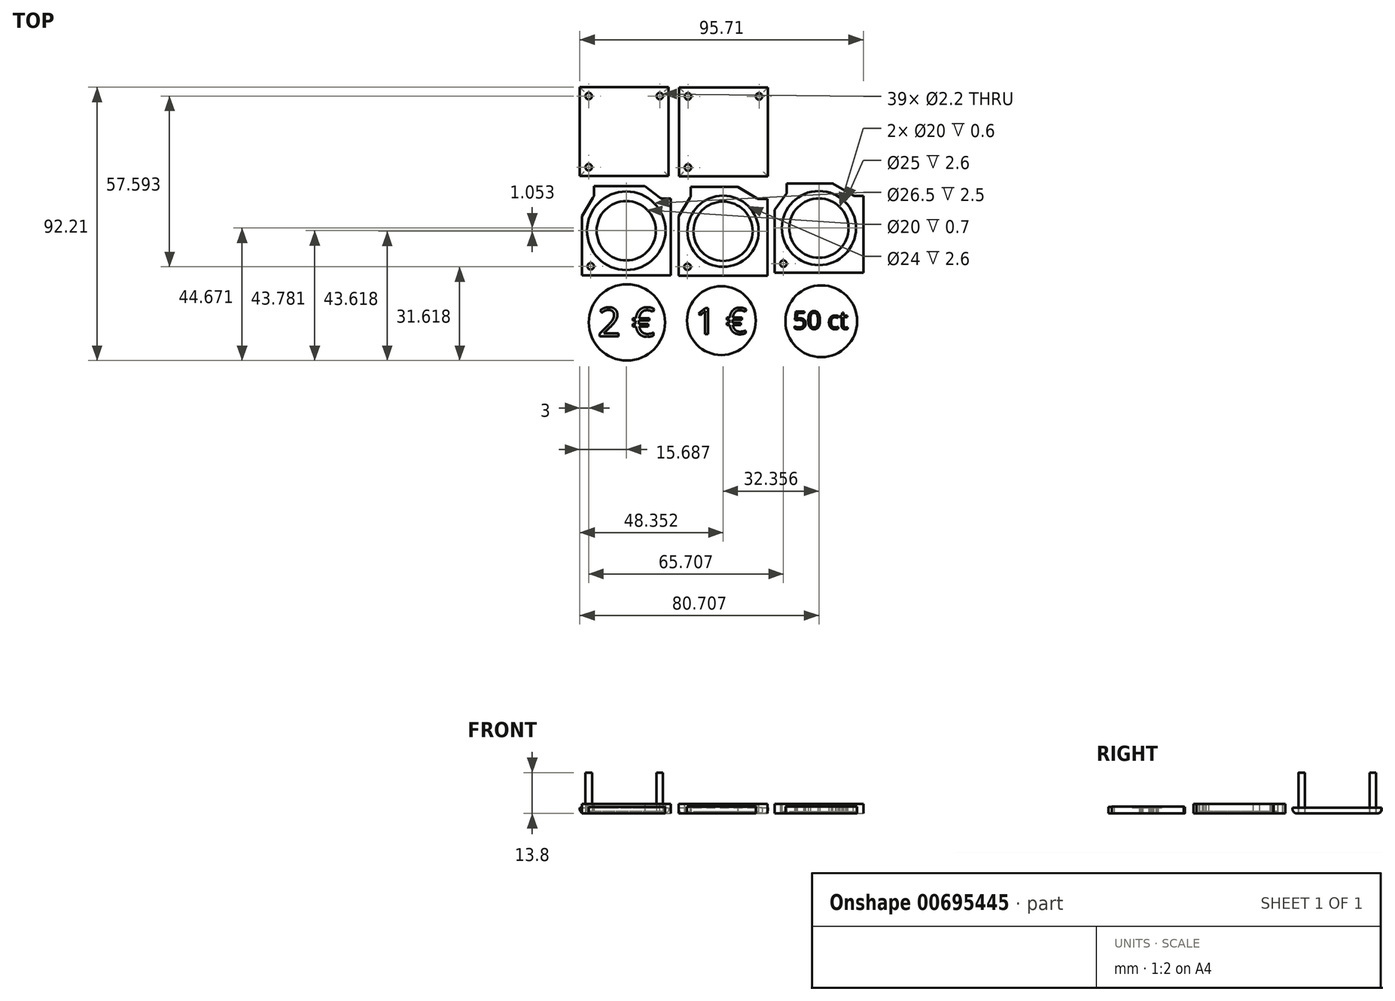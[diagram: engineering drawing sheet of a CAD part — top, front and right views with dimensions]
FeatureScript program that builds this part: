
annotation { "Feature Type Name" : "Feature", "Feature Type Description" : "" }
export const myFeature = defineFeature(function(context is Context, id is Id, definition is map)
    precondition{}
    {
        {
            var Q0;
            Q0=qCreatedBy(makeId("Top.planeOp"),FACE);
            var sketch = newSketch(context, id + "F0", { "sketchPlane" : qUnion([Q0])});
            skLineSegment(sketch, "E0.bottom", {"start": v(-47.79, 46.52) * mm, "end": v(-17.79, 46.52) * mm});
            skLineSegment(sketch, "E0.top", {"start": v(-47.79, 16.52) * mm, "end": v(-17.79, 16.52) * mm});
            skLineSegment(sketch, "E0.left", {"start": v(-47.79, 46.52) * mm, "end": v(-47.79, 16.52) * mm});
            skLineSegment(sketch, "E0.right", {"start": v(-17.79, 46.52) * mm, "end": v(-17.79, 16.52) * mm});
            skCircle(sketch, "E1", {"center": v(-44.79, 43.52) * mm, "radius": 1.1 * mm});
            skCircle(sketch, "E2", {"center": v(-20.79, 43.52) * mm, "radius": 1.1 * mm});
            skCircle(sketch, "E3", {"center": v(-44.79, 19.52) * mm, "radius": 1.1 * mm});
            skSolve(sketch);
        }
        {
            var Q0;
            Q0=makeQuery(id+"F0.imprint","IMPRINT",FACE,{"disambiguationData":[TD([[makeQuery(id+"F0.imprint","IMPRINT",EDGE,{"derivedFrom":sQuery(id+"F0.wireOp",EDGE,"E1")}),1.0]])]});
            var Q1;
            Q1=makeQuery(id+"F0.imprint","IMPRINT",FACE,{"disambiguationData":[TD([[makeQuery(id+"F0.imprint","IMPRINT",EDGE,{"derivedFrom":sQuery(id+"F0.wireOp",EDGE,"E2")}),1.0]])]});
            var Q2;
            Q2=makeQuery(id+"F0.imprint","IMPRINT",FACE,{"disambiguationData":[TD([[makeQuery(id+"F0.imprint","IMPRINT",EDGE,{"derivedFrom":sQuery(id+"F0.wireOp",EDGE,"E3")}),1.0]])]});
            extrude(context, id + "F1", {"entities" : qUnion([Q0, Q1, Q2]), "depth" : 13.8 * mm, "offsetDistance" : 25 * mm});
        }
        {
            var Q0;
            Q0 = qSketchRegion(id + "F0", true);
            extrude(context, id + "F2", {"entities" : qUnion([Q0]), "depth" : 2 * mm, "offsetDistance" : 25 * mm});
        }
        {
            var Q0;
            Q0=qCreatedBy(makeId("Top.planeOp"),FACE);
            var sketch = newSketch(context, id + "F3", { "sketchPlane" : qUnion([Q0])});
            skLineSegment(sketch, "E4.bottom", {"start": v(-14.28, 46.4) * mm, "end": v(15.72, 46.4) * mm});
            skLineSegment(sketch, "E4.top", {"start": v(-14.28, 16.4) * mm, "end": v(15.72, 16.4) * mm});
            skLineSegment(sketch, "E4.left", {"start": v(-14.28, 46.4) * mm, "end": v(-14.28, 16.4) * mm});
            skLineSegment(sketch, "E4.right", {"start": v(15.72, 46.4) * mm, "end": v(15.72, 16.4) * mm});
            skCircle(sketch, "E5", {"center": v(-11.28, 43.4) * mm, "radius": 1.1 * mm});
            skCircle(sketch, "E6", {"center": v(12.72, 43.4) * mm, "radius": 1.1 * mm});
            skCircle(sketch, "E7", {"center": v(-11.28, 19.4) * mm, "radius": 1.1 * mm});
            skSolve(sketch);
        }
        {
            var Q0;
            Q0=makeQuery(id+"F3.imprint","IMPRINT",FACE,{"disambiguationData":[TD([[makeQuery(id+"F3.imprint","IMPRINT",EDGE,{"derivedFrom":sQuery(id+"F3.wireOp",EDGE,"E5")}),1.0]])]});
            var Q1;
            Q1=makeQuery(id+"F3.imprint","IMPRINT",FACE,{"disambiguationData":[TD([[makeQuery(id+"F3.imprint","IMPRINT",EDGE,{"derivedFrom":sQuery(id+"F3.wireOp",EDGE,"E6")}),1.0]])]});
            var Q2;
            Q2=makeQuery(id+"F3.imprint","IMPRINT",FACE,{"disambiguationData":[TD([[makeQuery(id+"F3.imprint","IMPRINT",EDGE,{"derivedFrom":sQuery(id+"F3.wireOp",EDGE,"E7")}),1.0]])]});
            extrude(context, id + "F4", {"entities" : qUnion([Q0, Q1, Q2]), "depth" : 0.2 * mm, "offsetDistance" : 25 * mm});
        }
        {
            var Q0;
            Q0 = qSketchRegion(id + "F3", true);
            extrude(context, id + "F5", {"entities" : qUnion([Q0]), "depth" : 2 * mm, "offsetDistance" : 25 * mm});
        }
        {
            var Q0;
            Q0=makeQuery(id+"F2.opExtrude","CAP_EDGE",EDGE,{"disambiguationData":[OSD([sQuery(id+"F0.wireOp",EDGE,"E0.left")])],"isStart":true});
            var Q1;
            Q1=makeQuery(id+"F2.opExtrude","CAP_EDGE",EDGE,{"disambiguationData":[OSD([sQuery(id+"F0.wireOp",EDGE,"E0.bottom")])],"isStart":true});
            var Q2;
            Q2=makeQuery(id+"F2.opExtrude","CAP_EDGE",EDGE,{"disambiguationData":[OSD([sQuery(id+"F0.wireOp",EDGE,"E0.right")])],"isStart":true});
            var Q3;
            Q3=makeQuery(id+"F2.opExtrude","CAP_EDGE",EDGE,{"disambiguationData":[OSD([sQuery(id+"F0.wireOp",EDGE,"E0.top")])],"isStart":true});
            var Q4;
            Q4=makeQuery(id+"F5.opExtrude","CAP_EDGE",EDGE,{"disambiguationData":[OSD([sQuery(id+"F3.wireOp",EDGE,"E4.left")])],"isStart":true});
            var Q5;
            Q5=makeQuery(id+"F5.opExtrude","CAP_EDGE",EDGE,{"disambiguationData":[OSD([sQuery(id+"F3.wireOp",EDGE,"E4.bottom")])],"isStart":true});
            var Q6;
            Q6=makeQuery(id+"F5.opExtrude","CAP_EDGE",EDGE,{"disambiguationData":[OSD([sQuery(id+"F3.wireOp",EDGE,"E4.right")])],"isStart":true});
            var Q7;
            Q7=makeQuery(id+"F5.opExtrude","CAP_EDGE",EDGE,{"disambiguationData":[OSD([sQuery(id+"F3.wireOp",EDGE,"E4.top")])],"isStart":true});
            fillet(context, id + "F6", {"entities" : qUnion([Q0, Q1, Q2, Q3, Q4, Q5, Q6, Q7]), "radius" : 1.5 * mm, "tangentPropagation" : true, "allowEdgeOverflow" : false});
        }
        {
            var Q0;
            Q0=qCreatedBy(makeId("Top.planeOp"),FACE);
            var sketch = newSketch(context, id + "F7", { "sketchPlane" : qUnion([Q0])});
            skLineSegment(sketch, "E8.bottom", {"start": v(-47.1, 13.1) * mm, "end": v(-17.1, 13.1) * mm});
            skLineSegment(sketch, "E8.top", {"start": v(-47.1, -16.9) * mm, "end": v(-17.1, -16.9) * mm});
            skLineSegment(sketch, "E8.left", {"start": v(-47.1, 13.1) * mm, "end": v(-47.1, -16.9) * mm});
            skLineSegment(sketch, "E8.right", {"start": v(-17.1, 13.1) * mm, "end": v(-17.1, -16.9) * mm});
            skPoint(sketch, "E8.middle", {"position": v(-32.1, -1.9) * mm});
            skCircle(sketch, "E9", {"center": v(-44.1, -13.9) * mm, "radius": 1.1 * mm});
            skCircle(sketch, "E10", {"center": v(-32.1, -1.9) * mm, "radius": 10 * mm});
            skCircle(sketch, "E11", {"center": v(-32.1, -1.9) * mm, "radius": 13.25 * mm});
            skCircle(sketch, "E12", {"center": v(-44.1, 10.1) * mm, "radius": 1.1 * mm});
            skCircle(sketch, "E13", {"center": v(-20.1, 10.1) * mm, "radius": 1.1 * mm});
            skLineSegment(sketch, "E14", {"start": v(-43.38, 9.26) * mm, "end": v(-47.1, 3) * mm});
            skLineSegment(sketch, "E15", {"start": v(-43, 10.1) * mm, "end": v(-43, 13.1) * mm});
            skLineSegment(sketch, "E16", {"start": v(-20.1, 9) * mm, "end": v(-17.1, 9) * mm});
            skLineSegment(sketch, "E17", {"start": v(-20.83, 9.27) * mm, "end": v(-25.86, 13.1) * mm});
            skSolve(sketch);
        }
        {
            var Q0;
            {var subQ11=sQuery(id+"F7.wireOp",EDGE,"E8.top");Q0=makeQuery(id+"F7.imprint","IMPRINT",FACE,{"disambiguationData":[TD([[makeQuery(id+"F7.imprint","IMPRINT",EDGE,{"derivedFrom":subQ11}),1.0]])]});}
            extrude(context, id + "F8", {"entities" : qUnion([Q0]), "depth" : 3.2 * mm, "offsetDistance" : 25 * mm});
        }
        {
            var Q0;
            Q0=makeQuery(id+"F7.imprint","IMPRINT",FACE,{"disambiguationData":[TD([[makeQuery(id+"F7.imprint","IMPRINT",EDGE,{"derivedFrom":sQuery(id+"F7.wireOp",EDGE,"E10")}),-1.0]])]});
            extrude(context, id + "F9", {"entities" : qUnion([Q0]), "operationType" : NewBodyOperationType.ADD, "depth" : 0.7 * mm, "offsetDistance" : 25 * mm});
        }
        {
            var Q0;
            Q0=qCreatedBy(makeId("Top.planeOp"),FACE);
            var sketch = newSketch(context, id + "F10", { "sketchPlane" : qUnion([Q0])});
            skLineSegment(sketch, "E18.bottom", {"start": v(-14.44, 12.93) * mm, "end": v(15.56, 12.93) * mm});
            skLineSegment(sketch, "E18.top", {"start": v(-14.44, -17.07) * mm, "end": v(15.56, -17.07) * mm});
            skLineSegment(sketch, "E18.left", {"start": v(-14.44, 12.93) * mm, "end": v(-14.44, -17.07) * mm});
            skLineSegment(sketch, "E18.right", {"start": v(15.56, 12.93) * mm, "end": v(15.56, -17.07) * mm});
            skPoint(sketch, "E18.middle", {"position": v(0.56, -2.07) * mm});
            skCircle(sketch, "E19", {"center": v(-11.44, -14.07) * mm, "radius": 1.1 * mm});
            skCircle(sketch, "E20", {"center": v(0.56, -2.07) * mm, "radius": 10 * mm});
            skCircle(sketch, "E21", {"center": v(0.56, -2.07) * mm, "radius": 12 * mm});
            skCircle(sketch, "E22", {"center": v(-11.44, 9.93) * mm, "radius": 1.1 * mm});
            skCircle(sketch, "E23", {"center": v(12.56, 9.93) * mm, "radius": 1.1 * mm});
            skLineSegment(sketch, "E24", {"start": v(-10.65, 9.16) * mm, "end": v(-14.44, 3) * mm});
            skLineSegment(sketch, "E25", {"start": v(-10.37, 10.18) * mm, "end": v(-10.37, 12.93) * mm});
            skLineSegment(sketch, "E26", {"start": v(12.56, 8.83) * mm, "end": v(15.56, 8.83) * mm});
            skLineSegment(sketch, "E27", {"start": v(11.8, 9.13) * mm, "end": v(5.56, 12.93) * mm});
            skSolve(sketch);
        }
        {
            var Q0;
            Q0=makeQuery(id+"F10.imprint","IMPRINT",FACE,{"disambiguationData":[TD([[makeQuery(id+"F10.imprint","IMPRINT",EDGE,{"derivedFrom":sQuery(id+"F10.wireOp",EDGE,"E20")}),-1.0]])]});
            var Q1;
            {var subQ11=sQuery(id+"F10.wireOp",EDGE,"E18.top");Q1=makeQuery(id+"F10.imprint","IMPRINT",FACE,{"disambiguationData":[TD([[makeQuery(id+"F10.imprint","IMPRINT",EDGE,{"derivedFrom":subQ11}),1.0]])]});}
            extrude(context, id + "F11", {"entities" : qUnion([Q0, Q1]), "depth" : 0.6 * mm, "offsetDistance" : 25 * mm});
        }
        {
            var Q0;
            {var subQ11=sQuery(id+"F10.wireOp",EDGE,"E18.top");Q0=makeQuery(id+"F10.imprint","IMPRINT",FACE,{"disambiguationData":[TD([[makeQuery(id+"F10.imprint","IMPRINT",EDGE,{"derivedFrom":subQ11}),1.0]])]});}
            extrude(context, id + "F12", {"entities" : qUnion([Q0]), "operationType" : NewBodyOperationType.ADD, "depth" : 3.2 * mm, "offsetDistance" : 25 * mm});
        }
        {
            var Q0;
            Q0=qCreatedBy(makeId("Top.planeOp"),FACE);
            var sketch = newSketch(context, id + "F13", { "sketchPlane" : qUnion([Q0])});
            skLineSegment(sketch, "E28.bottom", {"start": v(17.92, 13.98) * mm, "end": v(47.92, 13.98) * mm});
            skLineSegment(sketch, "E28.top", {"start": v(17.92, -16.02) * mm, "end": v(47.92, -16.02) * mm});
            skLineSegment(sketch, "E28.left", {"start": v(17.92, 13.98) * mm, "end": v(17.92, -16.02) * mm});
            skLineSegment(sketch, "E28.right", {"start": v(47.92, 13.98) * mm, "end": v(47.92, -16.02) * mm});
            skPoint(sketch, "E28.middle", {"position": v(32.92, -1.02) * mm});
            skCircle(sketch, "E29", {"center": v(20.92, -13.02) * mm, "radius": 1.1 * mm});
            skCircle(sketch, "E30", {"center": v(32.92, -1.02) * mm, "radius": 10 * mm});
            skCircle(sketch, "E31", {"center": v(32.92, -1.02) * mm, "radius": 12.5 * mm});
            skCircle(sketch, "E32", {"center": v(20.92, 10.98) * mm, "radius": 1.1 * mm});
            skCircle(sketch, "E33", {"center": v(44.92, 10.98) * mm, "radius": 1.1 * mm});
            skLineSegment(sketch, "E34", {"start": v(21.65, 10.16) * mm, "end": v(17.92, 5.2) * mm});
            skLineSegment(sketch, "E35", {"start": v(22.02, 10.98) * mm, "end": v(22.02, 13.98) * mm});
            skLineSegment(sketch, "E36", {"start": v(44.92, 9.88) * mm, "end": v(47.92, 9.88) * mm});
            skLineSegment(sketch, "E37", {"start": v(44.32, 10.06) * mm, "end": v(37.59, 13.98) * mm});
            skSolve(sketch);
        }
        {
            var Q0;
            Q0=makeQuery(id+"F13.imprint","IMPRINT",FACE,{"disambiguationData":[TD([[makeQuery(id+"F13.imprint","IMPRINT",EDGE,{"derivedFrom":sQuery(id+"F13.wireOp",EDGE,"E30")}),-1.0]])]});
            extrude(context, id + "F14", {"entities" : qUnion([Q0]), "depth" : 0.6 * mm, "offsetDistance" : 25 * mm});
        }
        {
            var Q0;
            {var subQ13=sQuery(id+"F13.wireOp",EDGE,"E28.top");Q0=makeQuery(id+"F13.imprint","IMPRINT",FACE,{"disambiguationData":[TD([[makeQuery(id+"F13.imprint","IMPRINT",EDGE,{"derivedFrom":subQ13}),1.0]])]});}
            extrude(context, id + "F15", {"entities" : qUnion([Q0]), "operationType" : NewBodyOperationType.ADD, "depth" : 3.2 * mm, "offsetDistance" : 25 * mm});
        }
        {
            var Q0;
            Q0=qCreatedBy(makeId("Top.planeOp"),FACE);
            var sketch = newSketch(context, id + "F16", { "sketchPlane" : qUnion([Q0])});
            skCircle(sketch, "E38", {"center": v(-31.88, -32.84) * mm, "radius": 12.85 * mm});
            skCircle(sketch, "E39", {"center": v(0, -32.23) * mm, "radius": 11.6 * mm});
            skCircle(sketch, "E40", {"center": v(33.69, -32.44) * mm, "radius": 12.1 * mm});
            skText(sketch, "E41", { "text": "2 €", "fontName": "OpenSans-Regular.ttf"});
            skText(sketch, "E42", { "text": "1 €", "fontName": "OpenSans-Regular.ttf"});
            skText(sketch, "E43", { "text": "50 ct", "fontName": "OpenSans-Regular.ttf"});
            const initialGuessF16  = {"E41": [-0.04176, -0.03759, 1, 0, 0.00984], "E42": [-0.00881, -0.03674, 1, 0, 0.00886], "E43": [0.02414, -0.03505, 1, 0, 0.006]};
            skSetInitialGuess(sketch, initialGuessF16);
            skSolve(sketch);
        }
        {
            var Q0;
            Q0 = qSketchRegion(id + "F16", true);
            extrude(context, id + "F17", {"entities" : qUnion([Q0]), "depth" : 2.2 * mm, "offsetDistance" : 25 * mm});
        }
        {
            var Q0;
            Q0=makeQuery(id+"F16.imprint","IMPRINT",FACE,{"disambiguationData":[TD([[makeQuery(id+"F16.imprint","IMPRINT",EDGE,{"derivedFrom":sQuery(id+"F16.wireOp",EDGE,"E41.sketch_text.stroke-0")}),-1.0]])]});
            var Q1;
            Q1=makeQuery(id+"F16.imprint","IMPRINT",FACE,{"disambiguationData":[TD([[makeQuery(id+"F16.imprint","IMPRINT",EDGE,{"derivedFrom":sQuery(id+"F16.wireOp",EDGE,"E41.sketch_text.stroke-20")}),-1.0]])]});
            extrude(context, id + "F18", {"entities" : qUnion([Q0, Q1]), "operationType" : NewBodyOperationType.ADD, "depth" : 2 * mm, "offsetDistance" : 25 * mm});
        }
        {
            var Q0;
            Q0=makeQuery(id+"F16.imprint","IMPRINT",FACE,{"disambiguationData":[TD([[makeQuery(id+"F16.imprint","IMPRINT",EDGE,{"derivedFrom":sQuery(id+"F16.wireOp",EDGE,"E39")}),1.0]])]});
            extrude(context, id + "F19", {"entities" : qUnion([Q0]), "operationType" : NewBodyOperationType.ADD, "depth" : 2.3 * mm, "offsetDistance" : 25 * mm});
        }
        {
            var Q0;
            Q0=makeQuery(id+"F16.imprint","IMPRINT",FACE,{"disambiguationData":[TD([[makeQuery(id+"F16.imprint","IMPRINT",EDGE,{"derivedFrom":sQuery(id+"F16.wireOp",EDGE,"E42.sketch_text.stroke-0")}),-1.0]])]});
            var Q1;
            Q1=makeQuery(id+"F16.imprint","IMPRINT",FACE,{"disambiguationData":[TD([[makeQuery(id+"F16.imprint","IMPRINT",EDGE,{"derivedFrom":sQuery(id+"F16.wireOp",EDGE,"E42.sketch_text.stroke-9")}),-1.0]])]});
            extrude(context, id + "F20", {"entities" : qUnion([Q0, Q1]), "operationType" : NewBodyOperationType.ADD, "depth" : 2.1 * mm, "offsetDistance" : 25 * mm});
        }
        {
            var Q0;
            Q0=makeQuery(id+"F16.imprint","IMPRINT",FACE,{"disambiguationData":[TD([[makeQuery(id+"F16.imprint","IMPRINT",EDGE,{"derivedFrom":sQuery(id+"F16.wireOp",EDGE,"E40")}),1.0]])]});
            var Q1;
            Q1=makeQuery(id+"F16.imprint","IMPRINT",FACE,{"disambiguationData":[TD([[makeQuery(id+"F16.imprint","IMPRINT",EDGE,{"derivedFrom":sQuery(id+"F16.wireOp",EDGE,"E43.sketch_text.stroke-27")}),1.0]])]});
            extrude(context, id + "F21", {"entities" : qUnion([Q0, Q1]), "operationType" : NewBodyOperationType.ADD, "depth" : 2.35 * mm, "offsetDistance" : 25 * mm});
        }
        {
            var Q0;
            Q0=makeQuery(id+"F16.imprint","IMPRINT",FACE,{"disambiguationData":[TD([[makeQuery(id+"F16.imprint","IMPRINT",EDGE,{"derivedFrom":sQuery(id+"F16.wireOp",EDGE,"E43.sketch_text.stroke-0")}),-1.0]])]});
            var Q1;
            Q1=makeQuery(id+"F16.imprint","IMPRINT",FACE,{"disambiguationData":[TD([[makeQuery(id+"F16.imprint","IMPRINT",EDGE,{"derivedFrom":sQuery(id+"F16.wireOp",EDGE,"E43.sketch_text.stroke-19")}),-1.0]])]});
            var Q2;
            Q2=makeQuery(id+"F16.imprint","IMPRINT",FACE,{"disambiguationData":[TD([[makeQuery(id+"F16.imprint","IMPRINT",EDGE,{"derivedFrom":sQuery(id+"F16.wireOp",EDGE,"E43.sketch_text.stroke-35")}),-1.0]])]});
            var Q3;
            Q3=makeQuery(id+"F16.imprint","IMPRINT",FACE,{"disambiguationData":[TD([[makeQuery(id+"F16.imprint","IMPRINT",EDGE,{"derivedFrom":sQuery(id+"F16.wireOp",EDGE,"E43.sketch_text.stroke-50")}),-1.0]])]});
            extrude(context, id + "F22", {"entities" : qUnion([Q0, Q1, Q2, Q3]), "depth" : 2.15 * mm, "offsetDistance" : 25 * mm});
        }
    });
